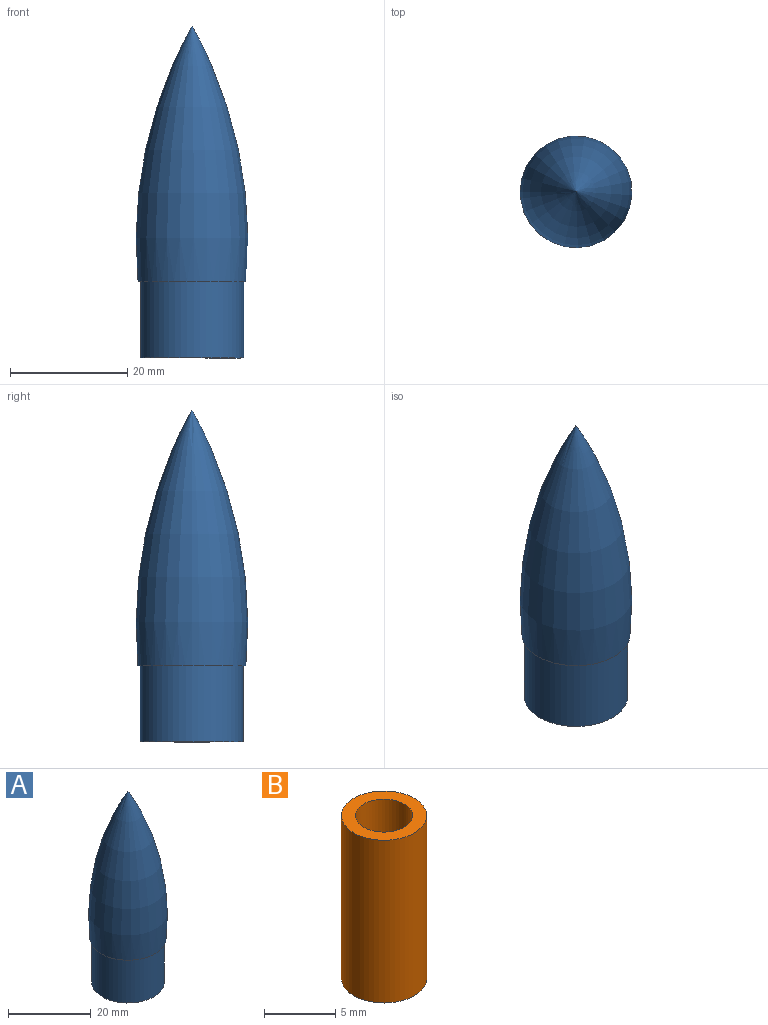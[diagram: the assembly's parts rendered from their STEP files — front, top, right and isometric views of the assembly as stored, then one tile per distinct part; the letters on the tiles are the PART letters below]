
ASSEMBLY  parts=2 mates=1
PART A: 7 faces, bbox 19.1x19.1x56.7 mm
  f0: plane 16.6x16.6mm, normal (0,0,1), area 25.3mm2, adj f1,f6
  f1: cylinder r=7.8mm len=15.6mm, axis (0,0,-1), area 686.1mm2, adj f0,f2
  f2: plane 17.6x17.6mm, normal (0,0,-1), area 52.2mm2, adj f1,f3
  f3: cylinder r=8.8mm len=17.6mm, axis (0,0,-1), area 718.8mm2, adj f2,f4
  f4: plane 18.43x18.43mm, normal (0,0,-1), area 23.5mm2, adj f3,f5
  f5: revolved ~43.67x19.09mm, area 1942mm2, adj f4
  f6: revolved ~40.58x17.09mm, area 1603.1mm2, adj f0
PART B: 4 faces, bbox 6x6x14 mm
  f0: cylinder r=2mm len=14mm, axis (0,0,-1), area 175.9mm2, adj f2,f3
  f1: cylinder r=3mm len=14mm, axis (0,0,-1), area 263.9mm2, adj f2,f3
  f2: plane 6x6mm, normal (0,0,1), area 15.7mm2, adj f0,f1
  f3: plane 6x6mm, normal (0,0,-1), area 15.7mm2, adj f0,f1
PLACE A t=(-5.11,-1.62,-0.02)mm
PLACE B t=(0.15,-1.62,25.25)mm
MATE planar A.f1 <-> B.f1  axis (0,0,-1) through (-5.11,-1.62,25.25)mm
